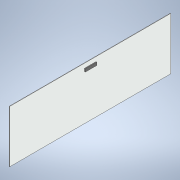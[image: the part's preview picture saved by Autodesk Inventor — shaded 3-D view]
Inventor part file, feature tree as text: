
AUTODESK INVENTOR PART (.ipt)
format: ipt  version: 2022 (Build 260153000, 153)  size: 119,296 bytes
history: native  units: mm
features: extrude x2, sketch x2, projected_geometry x1
ambient origin geometry x8: Origin, YZ Plane, XZ Plane, XY Plane, X Axis, Y Axis, Z Axis, Center Point
bodies: Solid1 (feature_tree)
feature tree (5):
  extrude  "Extrusion1"  Depth=1118.0mm
  extrude  "Extrusion2"  Depth=9.0mm
  sketch  "Sketch1"  dims[d0=363.0mm d1=1118.0mm]
  sketch  "Sketch2"  dims[d2=3.0mm d3=0.0mm d4=40.0mm d5=80.0mm d6=20.0mm d7=6.0mm d8=9.0mm d9=0.0mm d10=0.0mm]
  projected_geometry  "Projected Loop1"
